# Revit family: Misa_WC_dla_niepelnosprawnych_stal_szlachetna_matowa
name_source: partatom
category: Plumbing Fixtures
units: mm (PartAtom-declared; Revit-internal decimal feet)

## family parameters
Always vertical = Yes
Cut with Voids When Loaded = No
Host = Wall
Part Type = Normal
Room Calculation Point = No
Round Connector Dimension = Use Diameter
Shared = No

## types (1)
- URT207
    Depth / Glebokosc = 800 mm  [stored 2.62467 ft]
    Description = Misa WC posiada konstrukcję dostosowaną do potrzeb osób niepełnosprawnych. Brak ostrych krawędzi gwarantuje bezpieczeństwo użytkownikom. Wykonanie ze stali nierdzewnej zapewnia trwałość i solidność misy, a jej montaż do podłogi stabilność urządzenia. Jest odporna na wszelkie uszkodzenia mechaniczne oraz bardzo łatwa w czyszczeniu i konserwacji. WC ze stali nierdzewnej polecane jest do toalet publicznych o wysokim natężeniu ruchu.
    Height / Wysokosc = 466 mm  [stored 1.52887 ft]
    Manufacturer = FANECO.com
    Manufacturer code / Kod producenta = 5901764290698
    Material = Stal nierdzewna AISI 304
    Material finish / Wykonczenie = Stal nierdzewna 304 szczotkowana / polerowana
    Product code / Kod produktu = URT207
    Type Comments = Misa WC dla niepełnosprawnych stal szlachetna matowa
    URL = https://faneco.com
    Weight / Waga = 19 kg
    Width / Szerokosc = 355 mm  [stored 1.1647 ft]

note: [stored X ft] marks values corroborated as IEEE doubles in the binary element streams (Revit-internal decimal feet)

## geometry (parser evidence)
native form markers: Sweep x11
no freeform markers — native parametric forms only
